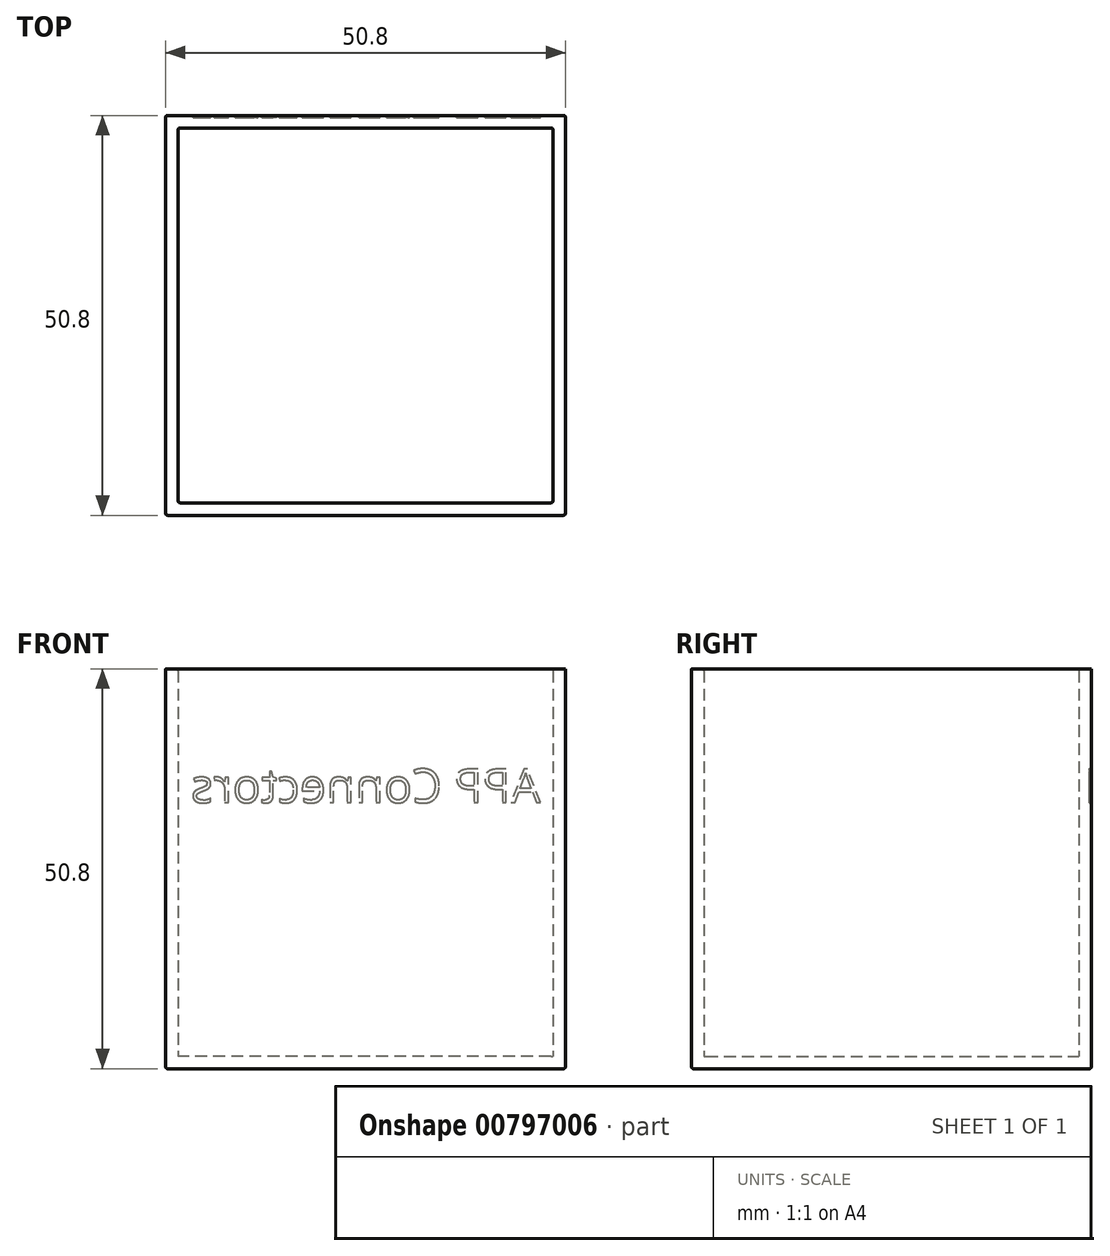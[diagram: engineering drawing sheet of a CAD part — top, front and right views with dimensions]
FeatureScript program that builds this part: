
annotation { "Feature Type Name" : "Feature", "Feature Type Description" : "" }
export const myFeature = defineFeature(function(context is Context, id is Id, definition is map)
    precondition{}
    {
        {
            var Q0;
            Q0=qCreatedBy(makeId("Top.planeOp"),FACE);
            var sketch = newSketch(context, id + "F0", { "sketchPlane" : qUnion([Q0])});
            skLineSegment(sketch, "E0.bottom", {"start": v(25.4, -25.4) * mm, "end": v(-25.4, -25.4) * mm});
            skLineSegment(sketch, "E0.top", {"start": v(25.4, 25.4) * mm, "end": v(-25.4, 25.4) * mm});
            skLineSegment(sketch, "E0.left", {"start": v(25.4, -25.4) * mm, "end": v(25.4, 25.4) * mm});
            skLineSegment(sketch, "E0.right", {"start": v(-25.4, -25.4) * mm, "end": v(-25.4, 25.4) * mm});
            skPoint(sketch, "E0.middle", {"position": v(0, 0) * mm});
            skSolve(sketch);
        }
        {
            var Q0;
            Q0=qSketchRegion(id+"F0",true);
            extrude(context, id + "F1", {"entities" : qUnion([Q0]), "depth" : 1.59 * mm, "offsetDistance" : 25.4 * mm});
        }
        {
            var Q0;
            Q0=makeQuery(id+"F1.opExtrude","CAP_FACE",FACE,{"disambiguationData":[OSD([sQuery(id+"F0.wireOp",EDGE,"E0.bottom"),sQuery(id+"F0.wireOp",EDGE,"E0.top"),sQuery(id+"F0.wireOp",EDGE,"E0.left"),sQuery(id+"F0.wireOp",EDGE,"E0.right")])],"isStart":false});
            var sketch = newSketch(context, id + "F2", { "sketchPlane" : qUnion([Q0])});
            skLineSegment(sketch, "E1.bottom", {"start": v(25.4, -25.4) * mm, "end": v(-25.4, -25.4) * mm});
            skLineSegment(sketch, "E1.top", {"start": v(25.4, 25.4) * mm, "end": v(-25.4, 25.4) * mm});
            skLineSegment(sketch, "E1.left", {"start": v(25.4, -25.4) * mm, "end": v(25.4, 25.4) * mm});
            skLineSegment(sketch, "E1.right", {"start": v(-25.4, -25.4) * mm, "end": v(-25.4, 25.4) * mm});
            skPoint(sketch, "E1.middle", {"position": v(0, 0) * mm});
            skLineSegment(sketch, "E2.0", {"start": v(23.81, 23.81) * mm, "end": v(-23.81, 23.81) * mm});
            skLineSegment(sketch, "E2.1", {"start": v(23.81, -23.81) * mm, "end": v(23.81, 23.81) * mm});
            skLineSegment(sketch, "E2.2", {"start": v(23.81, -23.81) * mm, "end": v(-23.81, -23.81) * mm});
            skLineSegment(sketch, "E2.3", {"start": v(-23.81, -23.81) * mm, "end": v(-23.81, 23.81) * mm});
            skSolve(sketch);
        }
        {
            var Q0;
            Q0=qSketchRegion(id+"F2",true);
            extrude(context, id + "F3", {"entities" : qUnion([Q0]), "operationType" : NewBodyOperationType.ADD, "depth" : 49.2 * mm, "offsetDistance" : 25.4 * mm});
        }
        {
            var Q0;
            Q0=makeQuery(id+"F3.opExtrude","CAP_EDGE",EDGE,{"disambiguationData":[OSD([sQuery(id+"F2.wireOp",EDGE,"E2.3")])],"isStart":true});
            var Q1;
            Q1=makeQuery(id+"F3.opExtrude","SWEPT_EDGE",EDGE,{"disambiguationData":[OSD([sQuery(id+"F2.wireOp",EDGE,"E2.2"),sQuery(id+"F2.wireOp",EDGE,"E2.3")])]});
            var Q2;
            Q2=makeQuery(id+"F3.opExtrude","CAP_EDGE",EDGE,{"disambiguationData":[OSD([sQuery(id+"F2.wireOp",EDGE,"E2.2")])],"isStart":true});
            var Q3;
            Q3=makeQuery(id+"F3.opExtrude","CAP_EDGE",EDGE,{"disambiguationData":[OSD([sQuery(id+"F2.wireOp",EDGE,"E2.3")])],"isStart":false});
            var Q4;
            Q4=makeQuery(id+"F3.opExtrude","CAP_EDGE",EDGE,{"disambiguationData":[OSD([sQuery(id+"F2.wireOp",EDGE,"E2.2")])],"isStart":false});
            var Q5;
            Q5=makeQuery(id+"F3.opExtrude","CAP_EDGE",EDGE,{"disambiguationData":[OSD([sQuery(id+"F2.wireOp",EDGE,"E2.0")])],"isStart":true});
            var Q6;
            Q6=makeQuery(id+"F3.opExtrude","SWEPT_EDGE",EDGE,{"disambiguationData":[OSD([sQuery(id+"F2.wireOp",EDGE,"E2.0"),sQuery(id+"F2.wireOp",EDGE,"E2.3")])]});
            var Q7;
            Q7=makeQuery(id+"F3.opExtrude","CAP_EDGE",EDGE,{"disambiguationData":[OSD([sQuery(id+"F2.wireOp",EDGE,"E2.0")])],"isStart":false});
            var Q8;
            Q8=makeQuery(id+"F3.opExtrude","SWEPT_EDGE",EDGE,{"disambiguationData":[OSD([sQuery(id+"F2.wireOp",EDGE,"E2.0"),sQuery(id+"F2.wireOp",EDGE,"E2.1")])]});
            var Q9;
            Q9=makeQuery(id+"F3.opExtrude","CAP_EDGE",EDGE,{"disambiguationData":[OSD([sQuery(id+"F2.wireOp",EDGE,"E2.1")])],"isStart":true});
            var Q10;
            Q10=makeQuery(id+"F3.opExtrude","CAP_EDGE",EDGE,{"disambiguationData":[OSD([sQuery(id+"F2.wireOp",EDGE,"E2.1")])],"isStart":false});
            var Q11;
            Q11=makeQuery(id+"F3.opExtrude","SWEPT_EDGE",EDGE,{"disambiguationData":[OSD([sQuery(id+"F2.wireOp",EDGE,"E2.1"),sQuery(id+"F2.wireOp",EDGE,"E2.2")])]});
            var Q12;
            Q12=makeQuery(id+"F3.boolean.opBoolean","MERGE",EDGE,{"derivedFrom":[makeQuery(id+"F1.opExtrude","SWEPT_EDGE",EDGE,{"disambiguationData":[OSD([sQuery(id+"F0.wireOp",EDGE,"E0.bottom"),sQuery(id+"F0.wireOp",EDGE,"E0.right")])]}),makeQuery(id+"F3.opExtrude","SWEPT_EDGE",EDGE,{"disambiguationData":[OSD([sQuery(id+"F2.wireOp",EDGE,"E1.bottom"),sQuery(id+"F2.wireOp",EDGE,"E1.right")])]})]});
            var Q13;
            Q13=makeQuery(id+"F3.boolean.opBoolean","MERGE",EDGE,{"derivedFrom":[makeQuery(id+"F1.opExtrude","SWEPT_EDGE",EDGE,{"disambiguationData":[OSD([sQuery(id+"F0.wireOp",EDGE,"E0.bottom"),sQuery(id+"F0.wireOp",EDGE,"E0.left")])]}),makeQuery(id+"F3.opExtrude","SWEPT_EDGE",EDGE,{"disambiguationData":[OSD([sQuery(id+"F2.wireOp",EDGE,"E1.bottom"),sQuery(id+"F2.wireOp",EDGE,"E1.left")])]})]});
            var Q14;
            Q14=makeQuery(id+"F3.boolean.opBoolean","MERGE",EDGE,{"derivedFrom":[makeQuery(id+"F1.opExtrude","SWEPT_EDGE",EDGE,{"disambiguationData":[OSD([sQuery(id+"F0.wireOp",EDGE,"E0.top"),sQuery(id+"F0.wireOp",EDGE,"E0.left")])]}),makeQuery(id+"F3.opExtrude","SWEPT_EDGE",EDGE,{"disambiguationData":[OSD([sQuery(id+"F2.wireOp",EDGE,"E1.top"),sQuery(id+"F2.wireOp",EDGE,"E1.left")])]})]});
            var Q15;
            Q15=makeQuery(id+"F3.boolean.opBoolean","MERGE",EDGE,{"derivedFrom":[makeQuery(id+"F1.opExtrude","SWEPT_EDGE",EDGE,{"disambiguationData":[OSD([sQuery(id+"F0.wireOp",EDGE,"E0.top"),sQuery(id+"F0.wireOp",EDGE,"E0.right")])]}),makeQuery(id+"F3.opExtrude","SWEPT_EDGE",EDGE,{"disambiguationData":[OSD([sQuery(id+"F2.wireOp",EDGE,"E1.top"),sQuery(id+"F2.wireOp",EDGE,"E1.right")])]})]});
            var Q16;
            Q16=makeQuery(id+"F1.opExtrude","CAP_EDGE",EDGE,{"disambiguationData":[OSD([sQuery(id+"F0.wireOp",EDGE,"E0.right")])],"isStart":true});
            var Q17;
            Q17=makeQuery(id+"F1.opExtrude","CAP_EDGE",EDGE,{"disambiguationData":[OSD([sQuery(id+"F0.wireOp",EDGE,"E0.bottom")])],"isStart":true});
            var Q18;
            Q18=makeQuery(id+"F1.opExtrude","CAP_EDGE",EDGE,{"disambiguationData":[OSD([sQuery(id+"F0.wireOp",EDGE,"E0.top")])],"isStart":true});
            var Q19;
            Q19=makeQuery(id+"F1.opExtrude","CAP_EDGE",EDGE,{"disambiguationData":[OSD([sQuery(id+"F0.wireOp",EDGE,"E0.left")])],"isStart":true});
            fillet(context, id + "F4", {"entities" : qUnion([Q0, Q1, Q2, Q3, Q4, Q5, Q6, Q7, Q8, Q9, Q10, Q11, Q12, Q13, Q14, Q15, Q16, Q17, Q18, Q19]), "radius" : 0.25 * mm, "tangentPropagation" : true, "allowEdgeOverflow" : false});
        }
        {
            var Q0;
            Q0=makeQuery(id+"F3.boolean.opBoolean","MERGE",FACE,{"derivedFrom":[makeQuery(id+"F1.opExtrude","SWEPT_FACE",FACE,{"disambiguationData":[OSD([sQuery(id+"F0.wireOp",EDGE,"E0.top")])]}),makeQuery(id+"F3.opExtrude","SWEPT_FACE",FACE,{"disambiguationData":[OSD([sQuery(id+"F2.wireOp",EDGE,"E1.top")])]})]});
            var sketch = newSketch(context, id + "F5", { "sketchPlane" : qUnion([Q0])});
            skText(sketch, "E3", { "text": "APP Connectors", "fontName": "OpenSans-Regular.ttf"});
            const initialGuessF5  = {"E3": [-0.02223, 0.0338, 1, 0, 0.0043]};
            skSetInitialGuess(sketch, initialGuessF5);
            skSolve(sketch);
        }
        {
            var Q0;
            Q0=qSketchRegion(id+"F5",true);
            extrude(context, id + "F6", {"entities" : qUnion([Q0]), "operationType" : NewBodyOperationType.REMOVE, "oppositeDirection" : true, "depth" : 0.25 * mm, "offsetDistance" : 25.4 * mm});
        }
    });
